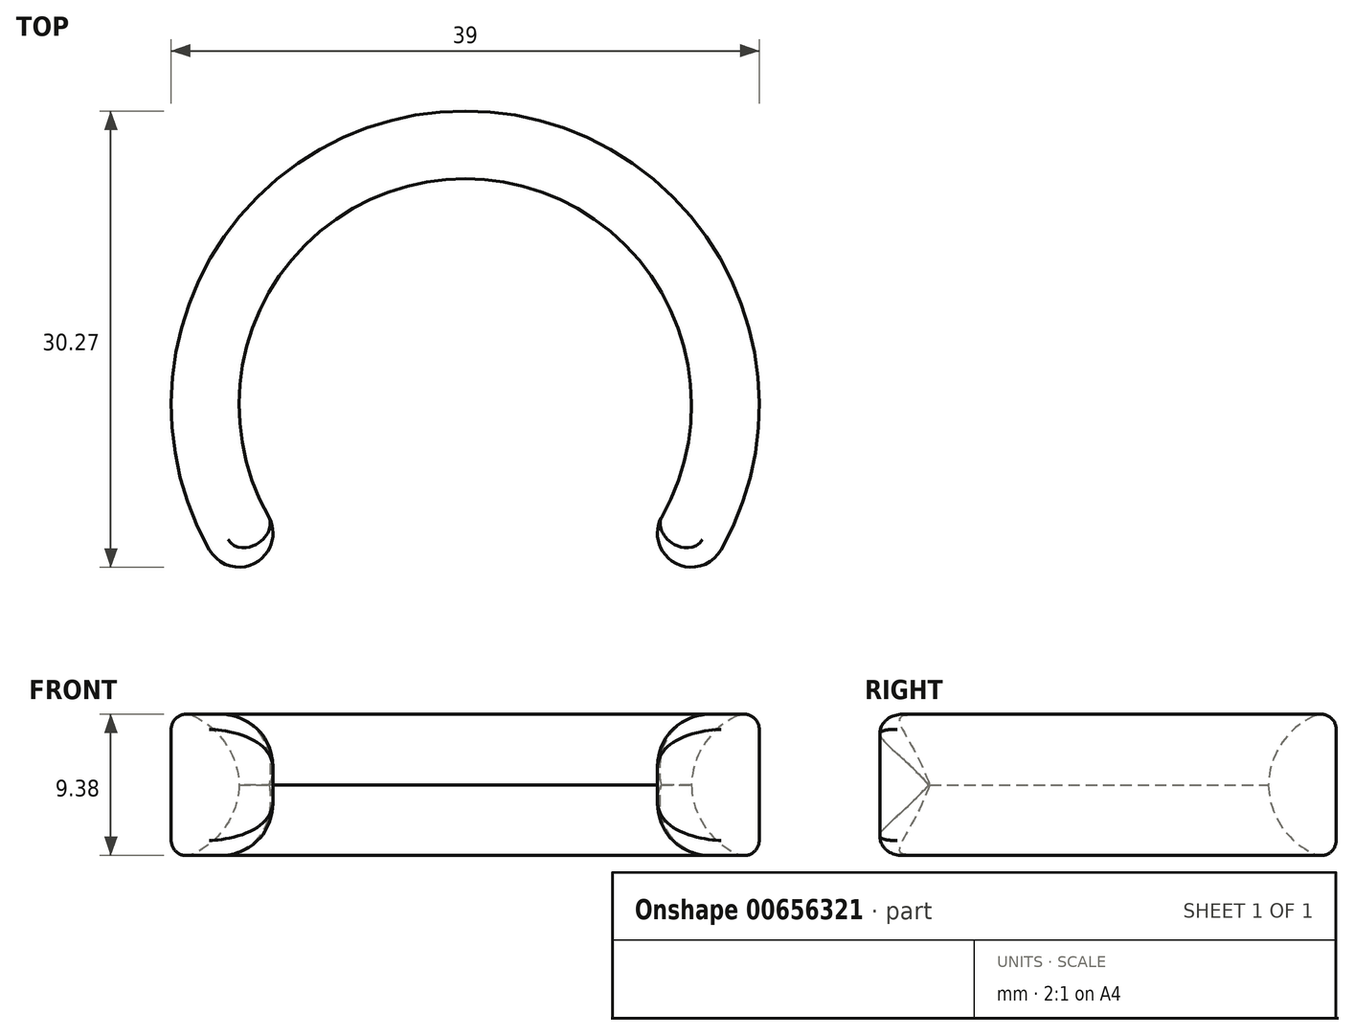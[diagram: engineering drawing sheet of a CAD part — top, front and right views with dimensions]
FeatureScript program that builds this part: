
annotation { "Feature Type Name" : "Feature", "Feature Type Description" : "" }
export const myFeature = defineFeature(function(context is Context, id is Id, definition is map)
    precondition{}
    {
        {
            var Q0;
            Q0=qCreatedBy(makeId("Top.planeOp"),FACE);
            var sketch = newSketch(context, id + "F0", { "sketchPlane" : qUnion([Q0])});
            skArc(sketch, "E0", {"start": v(16.96, -9.63) * mm, "mid": v(0, 19.5) * mm, "end": v(-16.96, -9.63) * mm});
            skArc(sketch, "E1", {"start": v(13.04, -7.4) * mm, "mid": v(0, 15) * mm, "end": v(-13.04, -7.4) * mm});
            skArc(sketch, "E2", {"start": v(13.04, -7.4) * mm, "mid": v(13.89, -10.47) * mm, "end": v(16.96, -9.63) * mm});
            skArc(sketch, "E3", {"start": v(-16.96, -9.63) * mm, "mid": v(-13.89, -10.47) * mm, "end": v(-13.04, -7.4) * mm});
            skPoint(sketch, "E4.orphan", {"position": v(-15, 0) * mm});
            skSolve(sketch);
        }
        {
            var Q0;
            Q0=makeQuery(id+"F0.imprint","IMPRINT",FACE,{"disambiguationData":[TD([[makeQuery(id+"F0.imprint","IMPRINT",EDGE,{"derivedFrom":sQuery(id+"F0.wireOp",EDGE,"E0")}),1.0]])]});
            extrude(context, id + "F1", {"entities" : qUnion([Q0]), "depth" : 10 * mm, "offsetDistance" : 25 * mm});
        }
        {
            var Q0;
            Q0=makeQuery(id+"F1.opExtrude","CAP_EDGE",EDGE,{"disambiguationData":[OSD([sQuery(id+"F0.wireOp",EDGE,"E1")])],"isStart":false});
            var Q1;
            Q1=makeQuery(id+"F1.opExtrude","CAP_EDGE",EDGE,{"disambiguationData":[OSD([sQuery(id+"F0.wireOp",EDGE,"E1")])],"isStart":true});
            var Q2;
            Q2=makeQuery(id+"F1.opExtrude","SWEPT_EDGE",EDGE,{"disambiguationData":[OSD([sQuery(id+"F0.wireOp",EDGE,"E1"),sQuery(id+"F0.wireOp",EDGE,"E3")])]});
            var Q3;
            Q3=makeQuery(id+"F1.opExtrude","SWEPT_EDGE",EDGE,{"disambiguationData":[OSD([sQuery(id+"F0.wireOp",EDGE,"E1"),sQuery(id+"F0.wireOp",EDGE,"E2")])]});
            fillet(context, id + "F2", {"entities" : qUnion([Q0, Q1, Q2, Q3]), "radius" : 5.2 * mm, "allowEdgeOverflow" : false});
        }
        {
            var Q0;
            Q0=makeQuery(id+"F2.opFillet","BLEND_EDGE",EDGE,{"blendedFrom":[makeQuery(id+"F1.opExtrude","CAP_EDGE",EDGE,{"disambiguationData":[OSD([sQuery(id+"F0.wireOp",EDGE,"E1")])],"isStart":false}),makeQuery(id+"F1.opExtrude","SWEPT_FACE",FACE,{"disambiguationData":[OSD([sQuery(id+"F0.wireOp",EDGE,"E2")])]})],"blendedInto":[makeQuery(id+"F1.opExtrude","SWEPT_FACE",FACE,{"disambiguationData":[OSD([sQuery(id+"F0.wireOp",EDGE,"E2")])]})]});
            var Q1;
            Q1=makeQuery(id+"F2.opFillet","BLEND_EDGE",EDGE,{"blendedFrom":[makeQuery(id+"F1.opExtrude","CAP_EDGE",EDGE,{"disambiguationData":[OSD([sQuery(id+"F0.wireOp",EDGE,"E1")])],"isStart":true}),makeQuery(id+"F1.opExtrude","SWEPT_FACE",FACE,{"disambiguationData":[OSD([sQuery(id+"F0.wireOp",EDGE,"E2")])]})],"blendedInto":[makeQuery(id+"F1.opExtrude","SWEPT_FACE",FACE,{"disambiguationData":[OSD([sQuery(id+"F0.wireOp",EDGE,"E2")])]})]});
            fillet(context, id + "F3", {"entities" : qUnion([Q0, Q1]), "radius" : 1 * mm, "tangentPropagation" : true, "allowEdgeOverflow" : false});
        }
    });
